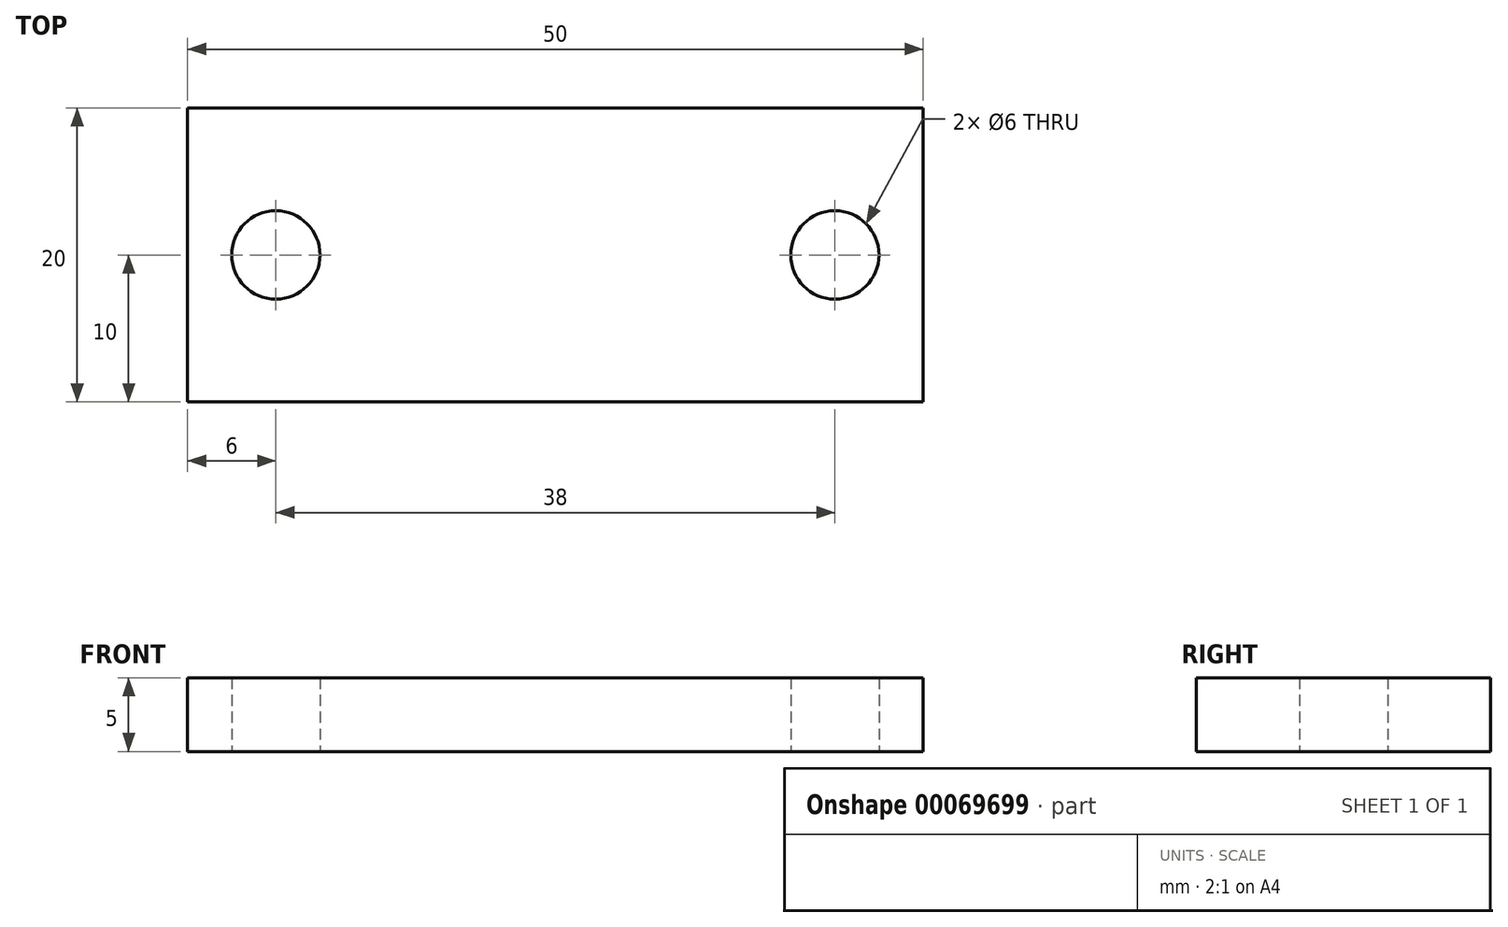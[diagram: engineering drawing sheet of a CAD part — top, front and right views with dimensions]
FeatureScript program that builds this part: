
annotation { "Feature Type Name" : "Feature", "Feature Type Description" : "" }
export const myFeature = defineFeature(function(context is Context, id is Id, definition is map)
    precondition{}
    {
        {
            var Q0;
            Q0=qCreatedBy(makeId("Top.planeOp"),FACE);
            var sketch = newSketch(context, id + "F0", { "sketchPlane" : qUnion([Q0])});
            skLineSegment(sketch, "E0.bottom", {"start": v(0, 0) * mm, "end": v(50, 0) * mm});
            skLineSegment(sketch, "E0.top", {"start": v(0, -20) * mm, "end": v(50, -20) * mm});
            skLineSegment(sketch, "E0.left", {"start": v(0, 0) * mm, "end": v(0, -20) * mm});
            skLineSegment(sketch, "E0.right", {"start": v(50, 0) * mm, "end": v(50, -20) * mm});
            skCircle(sketch, "E1", {"center": v(6, -10) * mm, "radius": 3 * mm});
            skCircle(sketch, "E2", {"center": v(44, -10) * mm, "radius": 3 * mm});
            skSolve(sketch);
        }
        {
            var Q0;
            Q0=makeQuery(id+"F0.imprint","IMPRINT",FACE,{"disambiguationData":[TD([[makeQuery(id+"F0.imprint","IMPRINT",EDGE,{"derivedFrom":sQuery(id+"F0.wireOp",EDGE,"E0.bottom")}),-1.0]])]});
            extrude(context, id + "F1", {"entities" : qUnion([Q0]), "depth" : 5 * mm});
        }
    });
